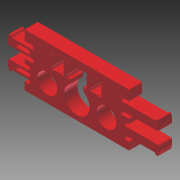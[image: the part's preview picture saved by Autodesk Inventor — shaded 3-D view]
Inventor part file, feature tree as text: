
AUTODESK INVENTOR PART (.ipt)
format: ipt  version: 2012 SP1 (Build 160190100, 190)  size: 227,328 bytes
history: native  units: in
note: dims shown in document units (in); Inventor stores cm internally (conversion verified against a paired STEP export)
features: other x3, extrude x1
ambient origin geometry x8: Origin, YZ Plane, XZ Plane, XY Plane, X Axis, Y Axis, Z Axis, Center Point
bodies: Solid1 (feature_tree)
feature tree (4):
  other  "skeleton.ipt"
  other  "STOCK_12MM"
  extrude  "Extrusion1"  Depth=0.3937in
  other  "THROUGH-CUT"
